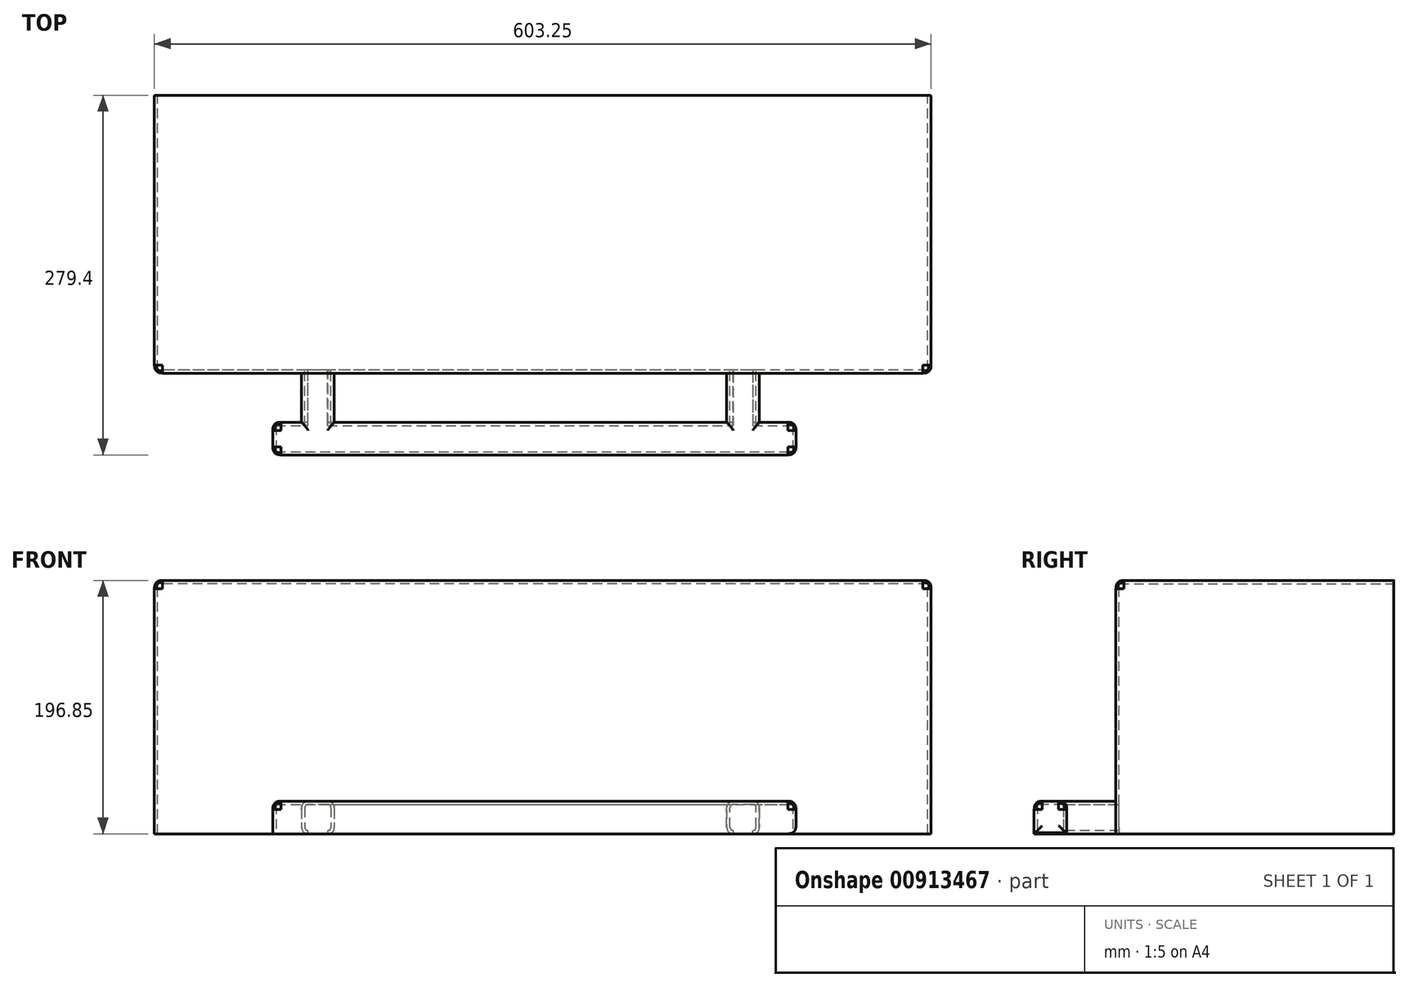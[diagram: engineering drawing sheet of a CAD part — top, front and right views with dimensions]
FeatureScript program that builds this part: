
annotation { "Feature Type Name" : "Feature", "Feature Type Description" : "" }
export const myFeature = defineFeature(function(context is Context, id is Id, definition is map)
    precondition{}
    {
        {
            var Q0;
            Q0=qCreatedBy(makeId("Front.planeOp"),FACE);
            var sketch = newSketch(context, id + "F0", { "sketchPlane" : qUnion([Q0])});
            skLineSegment(sketch, "E0.bottom", {"start": v(0, 0) * mm, "end": v(-603.25, 0) * mm});
            skLineSegment(sketch, "E0.top", {"start": v(0, 196.85) * mm, "end": v(-603.25, 196.85) * mm});
            skLineSegment(sketch, "E0.left", {"start": v(0, 0) * mm, "end": v(0, 196.85) * mm});
            skLineSegment(sketch, "E0.right", {"start": v(-603.25, 0) * mm, "end": v(-603.25, 196.85) * mm});
            skSolve(sketch);
        }
        {
            var Q0;
            Q0=makeQuery(id+"F0.imprint","IMPRINT",FACE,{"disambiguationData":[TD([[makeQuery(id+"F0.imprint","IMPRINT",EDGE,{"derivedFrom":sQuery(id+"F0.wireOp",EDGE,"E0.bottom")}),-1.0]])]});
            extrude(context, id + "F1", {"entities" : qUnion([Q0]), "depth" : 215.9 * mm, "offsetDistance" : 25.4 * mm});
        }
        {
            var Q0;
            Q0=qCreatedBy(makeId("Top.planeOp"),FACE);
            var sketch = newSketch(context, id + "F2", { "sketchPlane" : qUnion([Q0])});
            skLineSegment(sketch, "E1.bottom", {"start": v(-511.4, -254) * mm, "end": v(-105, -254) * mm});
            skLineSegment(sketch, "E1.top", {"start": v(-511.4, -279.4) * mm, "end": v(-105, -279.4) * mm});
            skLineSegment(sketch, "E1.left", {"start": v(-511.4, -254) * mm, "end": v(-511.4, -279.4) * mm});
            skLineSegment(sketch, "E1.right", {"start": v(-105, -254) * mm, "end": v(-105, -279.4) * mm});
            skLineSegment(sketch, "E2.bottom", {"start": v(-488.95, -254) * mm, "end": v(-463.55, -254) * mm});
            skLineSegment(sketch, "E2.top", {"start": v(-488.95, -215.33) * mm, "end": v(-463.55, -215.33) * mm});
            skLineSegment(sketch, "E2.left", {"start": v(-488.95, -254) * mm, "end": v(-488.95, -215.33) * mm});
            skLineSegment(sketch, "E2.right", {"start": v(-463.55, -254) * mm, "end": v(-463.55, -215.33) * mm});
            skLineSegment(sketch, "E3.bottom", {"start": v(-158.75, -215.33) * mm, "end": v(-133.35, -215.33) * mm});
            skLineSegment(sketch, "E3.top", {"start": v(-158.75, -254) * mm, "end": v(-133.35, -254) * mm});
            skLineSegment(sketch, "E3.left", {"start": v(-158.75, -215.33) * mm, "end": v(-158.75, -254) * mm});
            skLineSegment(sketch, "E3.right", {"start": v(-133.35, -215.33) * mm, "end": v(-133.35, -254) * mm});
            skSolve(sketch);
        }
        {
            var Q0;
            Q0=makeQuery(id+"F2.imprint","IMPRINT",FACE,{"disambiguationData":[TD([[makeQuery(id+"F2.imprint","IMPRINT",EDGE,{"derivedFrom":sQuery(id+"F2.wireOp",EDGE,"E1.top")}),1.0]])]});
            var Q1;
            Q1=makeQuery(id+"F2.imprint","IMPRINT",FACE,{"disambiguationData":[TD([[makeQuery(id+"F2.imprint","IMPRINT",EDGE,{"derivedFrom":sQuery(id+"F2.wireOp",EDGE,"E2.top")}),-1.0]])]});
            var Q2;
            Q2=makeQuery(id+"F2.imprint","IMPRINT",FACE,{"disambiguationData":[TD([[makeQuery(id+"F2.imprint","IMPRINT",EDGE,{"derivedFrom":sQuery(id+"F2.wireOp",EDGE,"E3.bottom")}),-1.0]])]});
            extrude(context, id + "F3", {"entities" : qUnion([Q0, Q1, Q2]), "operationType" : NewBodyOperationType.ADD, "depth" : 25.4 * mm, "offsetDistance" : 25.4 * mm});
        }
        {
            var Q0;
            Q0=makeQuery(id+"F3.opExtrude","CAP_EDGE",EDGE,{"disambiguationData":[OSD([sQuery(id+"F2.wireOp",EDGE,"E2.right")])],"isStart":false});
            var Q1;
            Q1=makeQuery(id+"F3.opExtrude","CAP_EDGE",EDGE,{"disambiguationData":[OSD([sQuery(id+"F2.wireOp",EDGE,"E2.left")])],"isStart":false});
            var Q2;
            Q2=makeQuery(id+"F3.opExtrude","CAP_EDGE",EDGE,{"disambiguationData":[OSD([sQuery(id+"F2.wireOp",EDGE,"E3.left")])],"isStart":false});
            var Q3;
            Q3=makeQuery(id+"F3.opExtrude","CAP_EDGE",EDGE,{"disambiguationData":[OSD([sQuery(id+"F2.wireOp",EDGE,"E3.right")])],"isStart":false});
            var Q4;
            Q4=makeQuery(id+"F3.opExtrude","CAP_EDGE",EDGE,{"disambiguationData":[OSD([sQuery(id+"F2.wireOp",EDGE,"E3.right")])],"isStart":true});
            var Q5;
            Q5=makeQuery(id+"F3.opExtrude","CAP_EDGE",EDGE,{"disambiguationData":[OSD([sQuery(id+"F2.wireOp",EDGE,"E2.right")])],"isStart":true});
            var Q6;
            Q6=makeQuery(id+"F3.opExtrude","CAP_EDGE",EDGE,{"disambiguationData":[OSD([sQuery(id+"F2.wireOp",EDGE,"E3.left")])],"isStart":true});
            var Q7;
            Q7=makeQuery(id+"F3.opExtrude","CAP_EDGE",EDGE,{"disambiguationData":[OSD([sQuery(id+"F2.wireOp",EDGE,"E2.left")])],"isStart":true});
            fillet(context, id + "F4", {"entities" : qUnion([Q0, Q1, Q2, Q3, Q4, Q5, Q6, Q7]), "radius" : 5.08 * mm, "tangentPropagation" : true, "allowEdgeOverflow" : false});
        }
        {
            var Q0;
            Q0=makeQuery(id+"F1.opExtrude","CAP_FACE",FACE,{"disambiguationData":[OSD([sQuery(id+"F0.wireOp",EDGE,"E0.bottom"),sQuery(id+"F0.wireOp",EDGE,"E0.top"),sQuery(id+"F0.wireOp",EDGE,"E0.left"),sQuery(id+"F0.wireOp",EDGE,"E0.right")])],"isStart":true});
            var Q1;
            Q1=makeQuery(id+"F3.boolean.opBoolean","MERGE",FACE,{"derivedFrom":[makeQuery(id+"F1.opExtrude","SWEPT_FACE",FACE,{"disambiguationData":[OSD([sQuery(id+"F0.wireOp",EDGE,"E0.bottom")])]}),makeQuery(id+"F3.opExtrude","CAP_FACE",FACE,{"disambiguationData":[OSD([sQuery(id+"F2.wireOp",EDGE,"E1.bottom"),sQuery(id+"F2.wireOp",EDGE,"E1.top"),sQuery(id+"F2.wireOp",EDGE,"E1.left"),sQuery(id+"F2.wireOp",EDGE,"E1.right"),sQuery(id+"F2.wireOp",EDGE,"E2.top"),sQuery(id+"F2.wireOp",EDGE,"E2.left"),sQuery(id+"F2.wireOp",EDGE,"E2.right"),sQuery(id+"F2.wireOp",EDGE,"E3.bottom"),sQuery(id+"F2.wireOp",EDGE,"E3.left"),sQuery(id+"F2.wireOp",EDGE,"E3.right")])],"isStart":true})]});
            shell(context, id + "F5", {"entities" : qUnion([Q0, Q1]), "thickness" : 2.54 * mm});
        }
        {
            var Q0;
            Q0=makeQuery(id+"F1.opExtrude","CAP_EDGE",EDGE,{"disambiguationData":[OSD([sQuery(id+"F0.wireOp",EDGE,"E0.top")])],"isStart":false});
            var Q1;
            Q1=makeQuery(id+"F1.opExtrude","SWEPT_EDGE",EDGE,{"disambiguationData":[OSD([sQuery(id+"F0.wireOp",EDGE,"E0.top"),sQuery(id+"F0.wireOp",EDGE,"E0.left")])]});
            var Q2;
            Q2=makeQuery(id+"F1.opExtrude","SWEPT_EDGE",EDGE,{"disambiguationData":[OSD([sQuery(id+"F0.wireOp",EDGE,"E0.top"),sQuery(id+"F0.wireOp",EDGE,"E0.right")])]});
            var Q3;
            Q3=makeQuery(id+"F1.opExtrude","CAP_EDGE",EDGE,{"disambiguationData":[OSD([sQuery(id+"F0.wireOp",EDGE,"E0.left")])],"isStart":false});
            var Q4;
            Q4=makeQuery(id+"F1.opExtrude","CAP_EDGE",EDGE,{"disambiguationData":[OSD([sQuery(id+"F0.wireOp",EDGE,"E0.right")])],"isStart":false});
            var Q5;
            Q5=makeQuery(id+"F3.opExtrude","CAP_EDGE",EDGE,{"disambiguationData":[OSD([sQuery(id+"F2.wireOp",EDGE,"E1.top")])],"isStart":false});
            var Q6;
            Q6=makeQuery(id+"F3.opExtrude","CAP_EDGE",EDGE,{"disambiguationData":[OSD([sQuery(id+"F2.wireOp",EDGE,"E1.right")])],"isStart":false});
            var Q7;
            Q7=makeQuery(id+"F3.opExtrude","CAP_EDGE",EDGE,{"disambiguationData":[OSD([sQuery(id+"F2.wireOp",EDGE,"E1.right")])],"isStart":true});
            var Q8;
            Q8=makeQuery(id+"F3.opExtrude","SWEPT_EDGE",EDGE,{"disambiguationData":[OSD([sQuery(id+"F2.wireOp",EDGE,"E1.bottom"),sQuery(id+"F2.wireOp",EDGE,"E1.right")])]});
            var Q9;
            Q9=makeQuery(id+"F3.opExtrude","SWEPT_EDGE",EDGE,{"disambiguationData":[OSD([sQuery(id+"F2.wireOp",EDGE,"E1.top"),sQuery(id+"F2.wireOp",EDGE,"E1.left")])]});
            var Q10;
            Q10=makeQuery(id+"F3.opExtrude","SWEPT_EDGE",EDGE,{"disambiguationData":[OSD([sQuery(id+"F2.wireOp",EDGE,"E1.top"),sQuery(id+"F2.wireOp",EDGE,"E1.right")])]});
            var Q11;
            Q11=makeQuery(id+"F3.opExtrude","CAP_EDGE",EDGE,{"disambiguationData":[OSD([sQuery(id+"F2.wireOp",EDGE,"E1.left")])],"isStart":false});
            var Q12;
            {var subQ0=sQuery(id+"F2.wireOp",EDGE,"E1.bottom");Q12=makeQuery(id+"F3.opExtrude","CAP_EDGE",EDGE,{"disambiguationData":[OSD([subQ0]),TDD([makeQuery(id+"F2.imprint","IMPRINT",EDGE,{"disambiguationData":[TD([[makeQuery(id+"F2.imprint","INTERSECT",VERTEX,{"derivedFrom":[subQ0,sQuery(id+"F2.wireOp",EDGE,"E2.right")]}),-1.0]])],"derivedFrom":subQ0})])],"isStart":false});}
            var Q13;
            {var subQ0=sQuery(id+"F2.wireOp",EDGE,"E1.bottom");Q13=makeQuery(id+"F3.opExtrude","CAP_EDGE",EDGE,{"disambiguationData":[OSD([subQ0]),TDD([makeQuery(id+"F2.imprint","IMPRINT",EDGE,{"disambiguationData":[TD([[makeQuery(id+"F2.imprint","INTERSECT",VERTEX,{"derivedFrom":[subQ0,sQuery(id+"F2.wireOp",EDGE,"E2.left")]}),1.0]])],"derivedFrom":subQ0})])],"isStart":false});}
            var Q14;
            Q14=makeQuery(id+"F3.opExtrude","SWEPT_EDGE",EDGE,{"disambiguationData":[OSD([sQuery(id+"F2.wireOp",EDGE,"E1.bottom"),sQuery(id+"F2.wireOp",EDGE,"E1.left")])]});
            var Q15;
            {var subQ0=sQuery(id+"F2.wireOp",EDGE,"E1.bottom");Q15=makeQuery(id+"F3.opExtrude","CAP_EDGE",EDGE,{"disambiguationData":[OSD([subQ0]),TDD([makeQuery(id+"F2.imprint","IMPRINT",EDGE,{"disambiguationData":[TD([[makeQuery(id+"F2.imprint","INTERSECT",VERTEX,{"derivedFrom":[subQ0,sQuery(id+"F2.wireOp",EDGE,"E1.right")]}),1.0]])],"derivedFrom":subQ0})])],"isStart":false});}
            fillet(context, id + "F6", {"entities" : qUnion([Q0, Q1, Q2, Q3, Q4, Q5, Q6, Q7, Q8, Q9, Q10, Q11, Q12, Q13, Q14, Q15]), "radius" : 6.35 * mm, "rho" : 0.5, "crossSection" : FilletCrossSection.CONIC, "allowEdgeOverflow" : false});
        }
    });
